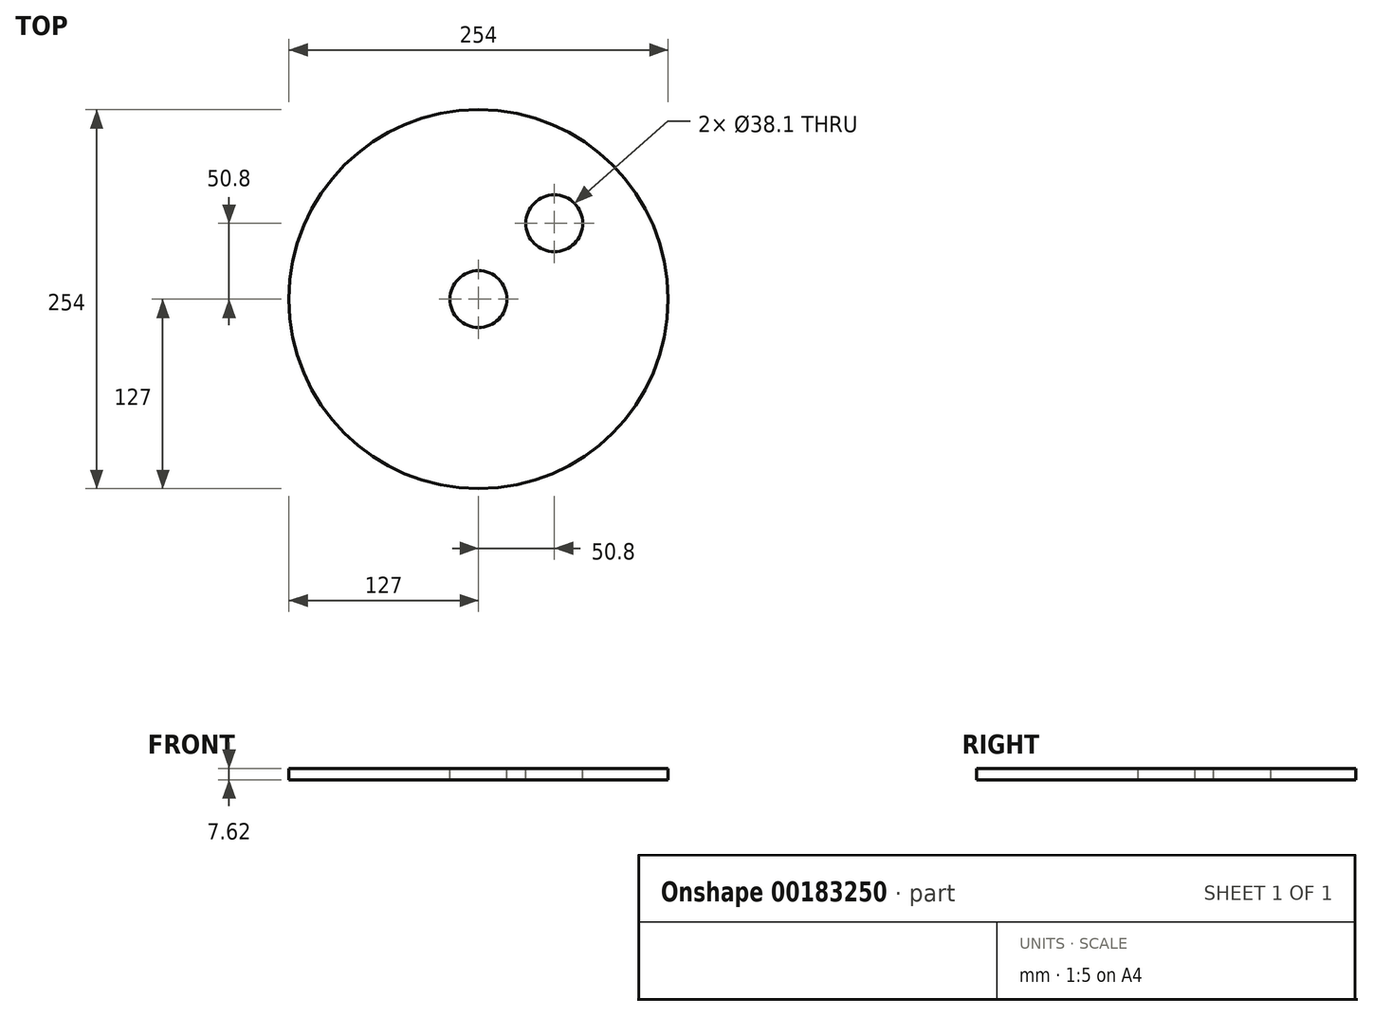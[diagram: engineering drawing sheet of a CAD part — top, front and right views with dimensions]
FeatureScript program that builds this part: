
annotation { "Feature Type Name" : "Feature", "Feature Type Description" : "" }
export const myFeature = defineFeature(function(context is Context, id is Id, definition is map)
    precondition{}
    {
        {
            var Q0;
            Q0=qCreatedBy(makeId("Top.planeOp"),FACE);
            var sketch = newSketch(context, id + "F0", { "sketchPlane" : qUnion([Q0])});
            skCircle(sketch, "E0", {"center": v(0, 0) * mm, "radius": 127 * mm});
            skSolve(sketch);
        }
        {
            var Q0;
            Q0=makeQuery(id+"F0.imprint","IMPRINT",FACE,{"disambiguationData":[TD([[makeQuery(id+"F0.imprint","IMPRINT",EDGE,{"derivedFrom":sQuery(id+"F0.wireOp",EDGE,"E0")}),1.0]])]});
            extrude(context, id + "F1", {"entities" : qUnion([Q0]), "depth" : 7.62 * mm});
        }
        {
            var Q0;
            Q0=makeQuery(id+"F1.opExtrude","CAP_FACE",FACE,{"disambiguationData":[OSD([sQuery(id+"F0.wireOp",EDGE,"E0")])],"isStart":false});
            var sketch = newSketch(context, id + "F2", { "sketchPlane" : qUnion([Q0])});
            skCircle(sketch, "E1", {"center": v(0, 0) * mm, "radius": 19.05 * mm});
            skCircle(sketch, "E2", {"center": v(50.8, 50.8) * mm, "radius": 19.05 * mm});
            skSolve(sketch);
        }
        {
            var Q0;
            Q0=makeQuery(id+"F2.imprint","IMPRINT",FACE,{"disambiguationData":[TD([[makeQuery(id+"F2.imprint","IMPRINT",EDGE,{"derivedFrom":sQuery(id+"F2.wireOp",EDGE,"E1")}),1.0]])]});
            var Q1;
            Q1=makeQuery(id+"F2.imprint","IMPRINT",FACE,{"disambiguationData":[TD([[makeQuery(id+"F2.imprint","IMPRINT",EDGE,{"derivedFrom":sQuery(id+"F2.wireOp",EDGE,"E2")}),1.0]])]});
            extrude(context, id + "F3", {"entities" : qUnion([Q0, Q1]), "operationType" : NewBodyOperationType.REMOVE, "oppositeDirection" : true, "depth" : 7.62 * mm});
        }
    });
